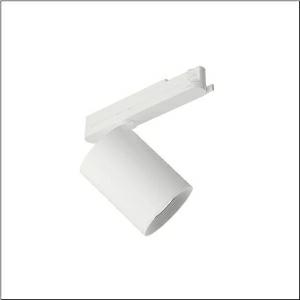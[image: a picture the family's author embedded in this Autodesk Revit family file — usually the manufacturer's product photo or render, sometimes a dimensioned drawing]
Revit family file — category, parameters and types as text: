
# Revit family: spot_11_51sd14mba5a
name_source: partatom
category: Lighting Fixtures
units: mm (PartAtom-declared; Revit-internal decimal feet)

## family parameters
Cut with Voids When Loaded = No
Host = Face
Light Source = No
Part Type = Normal
Room Calculation Point = No
Round Connector Dimension = Use Diameter
Shared = No

## types (1)
- --- (1 x LED, 7210 lm, 50.7 W, 2700K)
    Apparent Load = 51 VA
    CIE Flux Codes = 95 98 100 100 100
    Color Rendering = 90
    Color Temperature = 2700K
    Default Elevation = 1800 mm
    Description = Spot 11, directional spotlight, light control with lens, of PMMA, LED rated luminous flux: 5.550lm, light colour: 927, control gear: ECG Multilumen, with 3-phase adapter, mains connection: 220..240V, AC, 50/60Hz, of aluminium, traffic white (RAL 9016), length: 213mm, diameter: 105mm, protection rating (complete): IP20, insulation class (complete): insulation class I (protective earthing), certification: CE, impact resistance: IK02, permissible ambient temperature for indoor applications: -20..+40°C, packaging unit: 1 piece
    Height = 175 mm
    Lamp = 1 x LED
    Lamp Light Flux = 7210 lm
    Lamp Power = 50.7 W
    Lamp count = 1
    Length = 105 mm
    Luminous efficacy = 142 lm/W
    Manufacturer = Siteco
    ModVariant = No
    Model = 51SD14MBA5A
    Mounting Place = Ceiling
    Mounting Type = Pendant
    Number of Poles = 1
    OnlyDefault = Yes
    Power Factor = 1
    Product Name = Spot 11
    Product group = directional spotlight
    ProductGroupID = 906
    Protection Class = Protection class I
    Protection Degree = IP 20
    RLX_Detail_Level = 1
    RLX_Emergency_Light_Flux = 0 lm
    RLX_Emergency_Type = 0
    RLX_Emergency_Type_DB = No
    RlxData = <blob elided: 17673 chars, md5=18950177>
    Socket = socket
    Standby Power = 0 W
    System Light Flux = 7210 lm
    System Power = 51 W
    Type Comments = factory setting: luminous flux: 100 % | (ON | ON | ON | ON) | 1050 mA
    Type Image = l_1006697.jpg
    URL = http://relux.com
    VarID = @adj_147514
    Voltage = 0 V
    Weight = 0.00 kg
    Width = 0 mm  [stored 0 ft]

note: [stored X ft] marks values corroborated as IEEE doubles in the binary element streams (Revit-internal decimal feet)

## geometry (parser evidence)
native form markers: Blend x4, Sweep x8
no freeform markers — native parametric forms only
